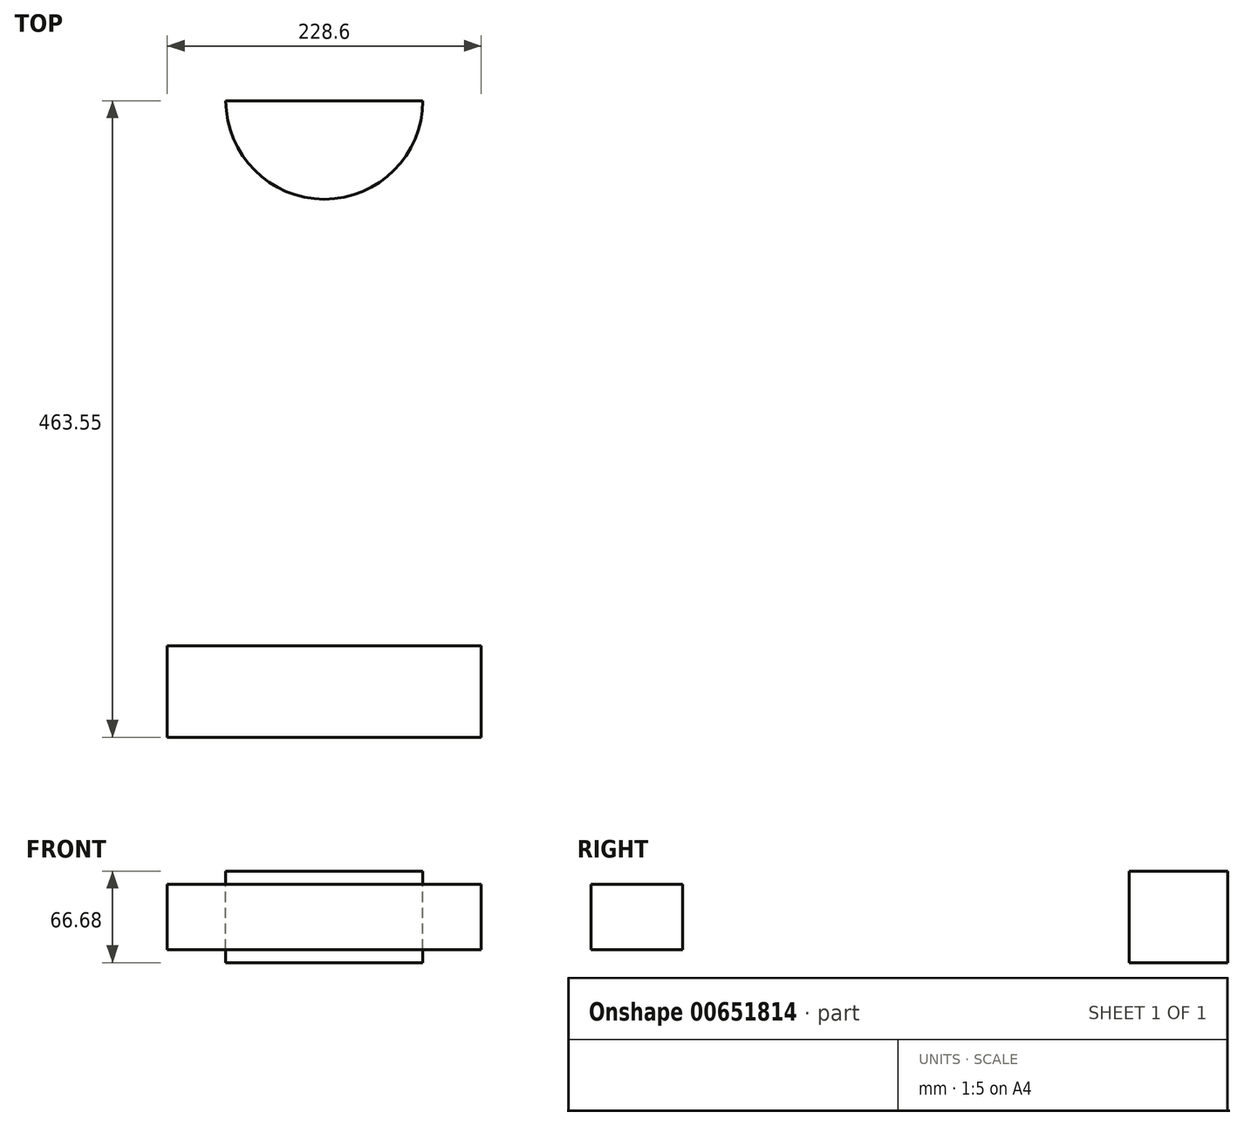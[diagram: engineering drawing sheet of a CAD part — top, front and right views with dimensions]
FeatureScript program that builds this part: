
annotation { "Feature Type Name" : "Feature", "Feature Type Description" : "" }
export const myFeature = defineFeature(function(context is Context, id is Id, definition is map)
    precondition{}
    {
        {
            var Q0;
            Q0=qCreatedBy(makeId("Front.planeOp"),FACE);
            var sketch = newSketch(context, id + "F0", { "sketchPlane" : qUnion([Q0])});
            skLineSegment(sketch, "E0.bottom", {"start": v(142.88, -33.34) * mm, "end": v(-142.88, -33.34) * mm});
            skLineSegment(sketch, "E0.top", {"start": v(142.88, 33.34) * mm, "end": v(-142.88, 33.34) * mm});
            skLineSegment(sketch, "E0.left", {"start": v(142.88, -33.34) * mm, "end": v(142.88, 33.34) * mm});
            skLineSegment(sketch, "E0.right", {"start": v(-142.88, -33.34) * mm, "end": v(-142.88, 33.34) * mm});
            skPoint(sketch, "E0.middle", {"position": v(0, 0) * mm});
            skSolve(sketch);
        }
        {
            var Q0;
            Q0=makeQuery(id+"F0.imprint","IMPRINT",FACE,{"disambiguationData":[TD([[makeQuery(id+"F0.imprint","IMPRINT",EDGE,{"derivedFrom":sQuery(id+"F0.wireOp",EDGE,"E0.bottom")}),-1.0]])]});
            extrude(context, id + "F1", {"entities" : qUnion([Q0]), "depth" : 508 * mm, "offsetDistance" : 25.4 * mm});
        }
        {
            var Q0;
            Q0=makeQuery(id+"F1.opExtrude","CAP_FACE",FACE,{"disambiguationData":[OSD([sQuery(id+"F0.wireOp",EDGE,"E0.bottom"),sQuery(id+"F0.wireOp",EDGE,"E0.top"),sQuery(id+"F0.wireOp",EDGE,"E0.left"),sQuery(id+"F0.wireOp",EDGE,"E0.right")])],"isStart":false});
            var sketch = newSketch(context, id + "F2", { "sketchPlane" : qUnion([Q0])});
            skLineSegment(sketch, "E1.bottom", {"start": v(114.3, -23.81) * mm, "end": v(-114.3, -23.81) * mm});
            skLineSegment(sketch, "E1.top", {"start": v(114.3, 23.81) * mm, "end": v(-114.3, 23.81) * mm});
            skLineSegment(sketch, "E1.left", {"start": v(114.3, -23.81) * mm, "end": v(114.3, 23.81) * mm});
            skLineSegment(sketch, "E1.right", {"start": v(-114.3, -23.81) * mm, "end": v(-114.3, 23.81) * mm});
            skPoint(sketch, "E1.middle", {"position": v(0, 0) * mm});
            skSolve(sketch);
        }
        {
            var Q0;
            Q0=makeQuery(id+"F2.imprint","IMPRINT",FACE,{"disambiguationData":[TD([[makeQuery(id+"F2.imprint","IMPRINT",EDGE,{"derivedFrom":sQuery(id+"F2.wireOp",EDGE,"E1.bottom")}),1.0]])]});
            extrude(context, id + "F3", {"entities" : qUnion([Q0]), "operationType" : NewBodyOperationType.REMOVE, "oppositeDirection" : true, "depth" : 66.67 * mm, "offsetDistance" : 25.4 * mm});
        }
        {
            var Q0;
            Q0=makeQuery(id+"F1.opExtrude","SWEPT_FACE",FACE,{"disambiguationData":[OSD([sQuery(id+"F0.wireOp",EDGE,"E0.top")])]});
            var sketch = newSketch(context, id + "F4", { "sketchPlane" : qUnion([Q0])});
            skLineSegment(sketch, "E2.bottom", {"start": v(-142.88, 0) * mm, "end": v(142.88, 0) * mm});
            skLineSegment(sketch, "E2.top", {"start": v(-142.88, -441.32) * mm, "end": v(142.88, -441.32) * mm});
            skLineSegment(sketch, "E2.left", {"start": v(-142.88, 0) * mm, "end": v(-142.88, -441.32) * mm});
            skLineSegment(sketch, "E2.right", {"start": v(142.88, 0) * mm, "end": v(142.88, -441.32) * mm});
            skLineSegment(sketch, "E3", {"start": v(-142.88, -44.45) * mm, "end": v(142.88, -44.45) * mm});
            skLineSegment(sketch, "E4.bottom", {"start": v(-142.88, 0) * mm, "end": v(-71.75, 0) * mm});
            skLineSegment(sketch, "E4.top", {"start": v(-142.88, -44.45) * mm, "end": v(-71.75, -44.45) * mm});
            skLineSegment(sketch, "E4.left", {"start": v(-142.88, 0) * mm, "end": v(-142.88, -44.45) * mm});
            skLineSegment(sketch, "E4.right", {"start": v(-71.75, 0) * mm, "end": v(-71.75, -44.45) * mm});
            skLineSegment(sketch, "E5.bottom", {"start": v(142.88, 0) * mm, "end": v(71.75, 0) * mm});
            skLineSegment(sketch, "E5.top", {"start": v(142.88, -44.45) * mm, "end": v(71.75, -44.45) * mm});
            skLineSegment(sketch, "E5.left", {"start": v(142.88, 0) * mm, "end": v(142.88, -44.45) * mm});
            skLineSegment(sketch, "E5.right", {"start": v(71.75, 0) * mm, "end": v(71.75, -44.45) * mm});
            skLineSegment(sketch, "E6", {"start": v(-142.88, 0) * mm, "end": v(-142.88, -508) * mm, "construction": true});
            skLineSegment(sketch, "E7", {"start": v(-142.88, -508) * mm, "end": v(142.88, -508) * mm, "construction": true});
            skLineSegment(sketch, "E8", {"start": v(142.88, -508) * mm, "end": v(142.87, 0) * mm, "construction": true});
            skLineSegment(sketch, "E9.bottom", {"start": v(0, -508) * mm, "end": v(-142.88, -508) * mm, "construction": true});
            skLineSegment(sketch, "E9.top", {"start": v(0, -276.83) * mm, "end": v(-142.88, -276.83) * mm, "construction": true});
            skLineSegment(sketch, "E9.left", {"start": v(0, -508) * mm, "end": v(0, -276.83) * mm, "construction": true});
            skLineSegment(sketch, "E9.right", {"start": v(-142.88, -508) * mm, "end": v(-142.88, -276.83) * mm, "construction": true});
            skCircle(sketch, "E10", {"center": v(0, -276.83) * mm, "radius": 89.3 * mm});
            skLineSegment(sketch, "E11", {"start": v(-142.88, -223.04) * mm, "end": v(142.88, -223.04) * mm, "construction": true});
            skArc(sketch, "E12", {"start": v(-71.75, -44.45) * mm, "mid": v(0, -116.2) * mm, "end": v(71.75, -44.45) * mm});
            skSolve(sketch);
        }
        {
            var Q0;
            Q0=makeQuery(id+"F4.imprint","IMPRINT",FACE,{"disambiguationData":[TD([[makeQuery(id+"F4.imprint","IMPRINT",EDGE,{"derivedFrom":sQuery(id+"F4.wireOp",EDGE,"E10")}),1.0]])]});
            var Q1;
            Q1=makeQuery(id+"F4.imprint","IMPRINT",FACE,{"disambiguationData":[TD([[makeQuery(id+"F4.imprint","IMPRINT",EDGE,{"derivedFrom":sQuery(id+"F4.wireOp",EDGE,"E3")}),-1.0]])]});
            var Q2;
            Q2=makeQuery(id+"F4.imprint","IMPRINT",FACE,{"disambiguationData":[TD([[makeQuery(id+"F4.imprint","IMPRINT",EDGE,{"derivedFrom":sQuery(id+"F4.wireOp",EDGE,"E2.bottom")}),1.0]])]});
            extrude(context, id + "F5", {"entities" : qUnion([Q0, Q1, Q2]), "operationType" : NewBodyOperationType.REMOVE, "endBound" : BoundingType.THROUGH_ALL, "oppositeDirection" : true, "depth" : 182.88 * mm, "offsetDistance" : 25.4 * mm});
        }
    });
